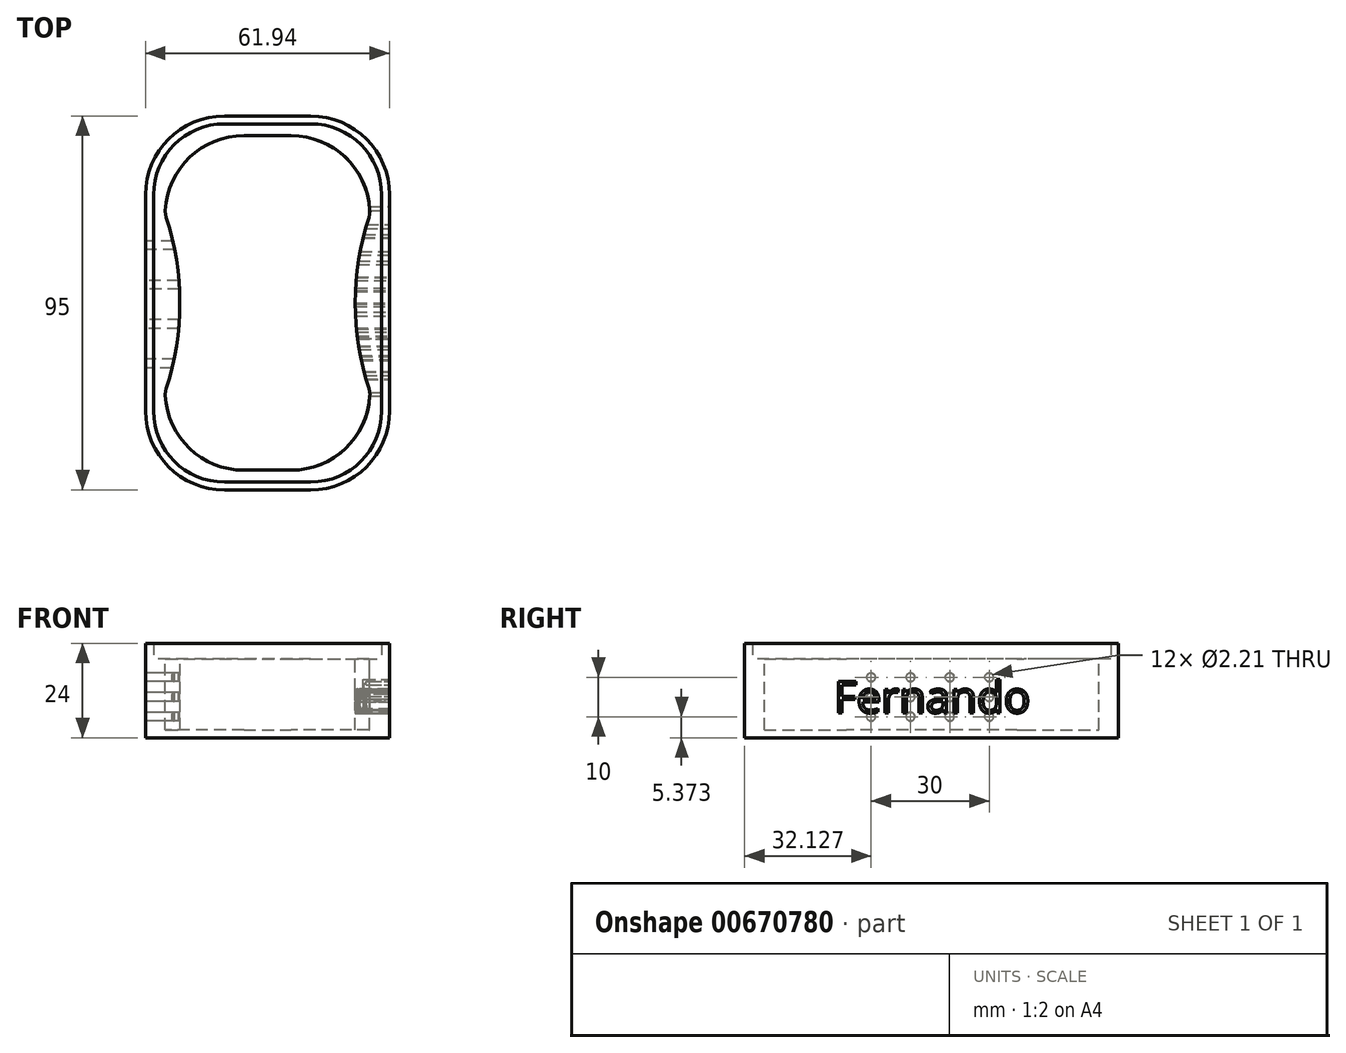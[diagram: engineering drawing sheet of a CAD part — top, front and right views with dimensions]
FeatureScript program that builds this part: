
annotation { "Feature Type Name" : "Feature", "Feature Type Description" : "" }
export const myFeature = defineFeature(function(context is Context, id is Id, definition is map)
    precondition{}
    {
        {
            var Q0;
            Q0=qCreatedBy(makeId("Top.planeOp"),FACE);
            var Q1;
            Q1 = qBodyType(qCreatedBy(id + "F1" ,EDGE), BodyType.WIRE);
            var Q2;
            Q2 = qBodyType(qCreatedBy(id + "F2" ,EDGE), BodyType.WIRE);
            cPlane(context, id + "F0", {"entities" : qUnion([Q0, Q1, Q2]), "cplaneType" : CPlaneType.OFFSET, "offset" : 20 * mm, "oppositeDirection" : true, "width" : 150 * mm, "height" : 150 * mm});
        }
        {
            var Q0;
            Q0=qCreatedBy(makeId("Top.planeOp"),FACE);
            var sketch = newSketch(context, id + "F1", { "sketchPlane" : qUnion([Q0])});
            skLineSegment(sketch, "E0", {"start": v(0, 100) * mm, "end": v(0, -100) * mm, "construction": true});
            skLineSegment(sketch, "E1", {"start": v(17.97, 4.54) * mm, "end": v(17.97, 0) * mm, "construction": true});
            skLineSegment(sketch, "E2", {"start": v(-100, 0) * mm, "end": v(100, 0) * mm, "construction": true});
            skLineSegment(sketch, "E3.bottom", {"start": v(20, 0) * mm, "end": v(32, 0) * mm});
            skLineSegment(sketch, "E3.top", {"start": v(20, 85) * mm, "end": v(32, 85) * mm});
            skPoint(sketch, "E4.visualSharp", {"position": v(0, 85) * mm});
            skArc(sketch, "E4.filletArc", {"start": v(20, 85) * mm, "mid": v(6.22, 79.5) * mm, "end": v(0.03, 66) * mm});
            skPoint(sketch, "E5.visualSharp", {"position": v(52, 85) * mm});
            skArc(sketch, "E5.filletArc", {"start": v(51.97, 66) * mm, "mid": v(45.78, 79.5) * mm, "end": v(32, 85) * mm});
            skPoint(sketch, "E6.visualSharp", {"position": v(0, 0) * mm});
            skArc(sketch, "E6.filletArc", {"start": v(0.03, 19) * mm, "mid": v(6.22, 5.5) * mm, "end": v(20, 0) * mm});
            skPoint(sketch, "E7.visualSharp", {"position": v(52, 0) * mm});
            skArc(sketch, "E7.filletArc", {"start": v(32, 0) * mm, "mid": v(45.78, 5.5) * mm, "end": v(51.97, 19) * mm});
            skArc(sketch, "E8", {"start": v(0.27, 20.8) * mm, "mid": v(3.71, 42.5) * mm, "end": v(0.27, 64.2) * mm});
            skArc(sketch, "E9", {"start": v(51.73, 64.2) * mm, "mid": v(48.29, 42.5) * mm, "end": v(51.73, 20.8) * mm});
            skPoint(sketch, "E10.visualSharp", {"position": v(0, 65) * mm});
            skArc(sketch, "E10.filletArc", {"start": v(0.03, 66) * mm, "mid": v(0.06, 65.1) * mm, "end": v(0.27, 64.2) * mm});
            skPoint(sketch, "E11.visualSharp", {"position": v(52, 65) * mm});
            skArc(sketch, "E11.filletArc", {"start": v(51.73, 64.2) * mm, "mid": v(51.94, 65.1) * mm, "end": v(51.97, 66) * mm});
            skPoint(sketch, "E12.visualSharp", {"position": v(52, 20) * mm});
            skArc(sketch, "E12.filletArc", {"start": v(51.97, 19) * mm, "mid": v(51.94, 19.9) * mm, "end": v(51.73, 20.8) * mm});
            skPoint(sketch, "E13.visualSharp", {"position": v(0, 20) * mm});
            skArc(sketch, "E13.filletArc", {"start": v(0.27, 20.8) * mm, "mid": v(0.06, 19.9) * mm, "end": v(0.03, 19) * mm});
            skSolve(sketch);
        }
        {
            var Q0;
            Q0=qCreatedBy(id+"F0.planeOp",FACE);
            var sketch = newSketch(context, id + "F2", { "sketchPlane" : qUnion([Q0])});
            skLineSegment(sketch, "E14.bottom", {"start": v(-4.97, 90) * mm, "end": v(56.97, 90) * mm});
            skLineSegment(sketch, "E14.top", {"start": v(-4.97, -5) * mm, "end": v(56.97, -5) * mm});
            skLineSegment(sketch, "E14.left", {"start": v(-4.97, 90) * mm, "end": v(-4.97, -5) * mm});
            skLineSegment(sketch, "E14.right", {"start": v(56.97, 90) * mm, "end": v(56.97, -5) * mm});
            skSolve(sketch);
        }
        {
            var Q0;
            Q0 = qSketchRegion(id + "F2", true);
            extrude(context, id + "F3", {"entities" : qUnion([Q0]), "depth" : 20 * mm, "offsetDistance" : 25 * mm});
        }
        {
            var Q0;
            Q0=makeQuery(id+"F3.opExtrude","SWEPT_EDGE",EDGE,{"disambiguationData":[OSD([sQuery(id+"F2.wireOp",EDGE,"E14.bottom"),sQuery(id+"F2.wireOp",EDGE,"E14.left")])]});
            var Q1;
            Q1=makeQuery(id+"F3.opExtrude","SWEPT_EDGE",EDGE,{"disambiguationData":[OSD([sQuery(id+"F2.wireOp",EDGE,"E14.top"),sQuery(id+"F2.wireOp",EDGE,"E14.left")])]});
            var Q2;
            Q2=makeQuery(id+"F3.opExtrude","SWEPT_EDGE",EDGE,{"disambiguationData":[OSD([sQuery(id+"F2.wireOp",EDGE,"E14.top"),sQuery(id+"F2.wireOp",EDGE,"E14.right")])]});
            var Q3;
            Q3=makeQuery(id+"F3.opExtrude","SWEPT_EDGE",EDGE,{"disambiguationData":[OSD([sQuery(id+"F2.wireOp",EDGE,"E14.bottom"),sQuery(id+"F2.wireOp",EDGE,"E14.right")])]});
            fillet(context, id + "F4", {"entities" : qUnion([Q0, Q1, Q2, Q3]), "radius" : 20 * mm, "tangentPropagation" : true, "allowEdgeOverflow" : false});
        }
        {
            var Q0;
            Q0 = qSketchRegion(id + "F1", true);
            extrude(context, id + "F5", {"entities" : qUnion([Q0]), "operationType" : NewBodyOperationType.REMOVE, "oppositeDirection" : true, "depth" : 18 * mm, "offsetDistance" : 25 * mm});
        }
        {
            var Q0;
            Q0=makeQuery(id+"F3.opExtrude","SWEPT_FACE",FACE,{"disambiguationData":[OSD([sQuery(id+"F2.wireOp",EDGE,"E14.right")])]});
            var sketch = newSketch(context, id + "F6", { "sketchPlane" : qUnion([Q0])});
            skText(sketch, "E15", { "text": "Fernando\n", "fontName": "OpenSans-Regular.ttf"});
            const initialGuessF6  = {"E15": [0.0177, -0.01364, 1, 0, 0.008]};
            skSetInitialGuess(sketch, initialGuessF6);
            skSolve(sketch);
        }
        {
            var Q0;
            Q0 = qSketchRegion(id + "F6", true);
            extrude(context, id + "F7", {"entities" : qUnion([Q0]), "operationType" : NewBodyOperationType.REMOVE, "oppositeDirection" : true, "depth" : 18 * mm, "offsetDistance" : 25 * mm});
        }
        {
            var Q0;
            Q0=makeQuery(id+"F3.opExtrude","SWEPT_FACE",FACE,{"disambiguationData":[OSD([sQuery(id+"F2.wireOp",EDGE,"E14.left")])]});
            var sketch = newSketch(context, id + "F8", { "sketchPlane" : qUnion([Q0])});
            skCircle(sketch, "E16", {"center": v(-57.13, -14.63) * mm, "radius": 1.1 * mm});
            skCircle(sketch, "E17.0.1.0", {"center": v(-57.13, -9.63) * mm, "radius": 1.1 * mm});
            skCircle(sketch, "E17.0.2.0", {"center": v(-57.13, -4.63) * mm, "radius": 1.1 * mm});
            skCircle(sketch, "E17.1.0.0", {"center": v(-47.13, -14.63) * mm, "radius": 1.1 * mm});
            skCircle(sketch, "E17.1.1.0", {"center": v(-47.13, -9.63) * mm, "radius": 1.1 * mm});
            skCircle(sketch, "E17.1.2.0", {"center": v(-47.13, -4.63) * mm, "radius": 1.1 * mm});
            skCircle(sketch, "E17.2.0.0", {"center": v(-37.13, -14.63) * mm, "radius": 1.1 * mm});
            skCircle(sketch, "E17.2.1.0", {"center": v(-37.13, -9.63) * mm, "radius": 1.1 * mm});
            skCircle(sketch, "E17.2.2.0", {"center": v(-37.13, -4.63) * mm, "radius": 1.1 * mm});
            skCircle(sketch, "E17.3.0.0", {"center": v(-27.13, -14.63) * mm, "radius": 1.1 * mm});
            skCircle(sketch, "E17.3.1.0", {"center": v(-27.13, -9.63) * mm, "radius": 1.1 * mm});
            skCircle(sketch, "E17.3.2.0", {"center": v(-27.13, -4.63) * mm, "radius": 1.1 * mm});
            skLineSegment(sketch, "E17.direction1", {"start": v(-57.13, -14.63) * mm, "end": v(-47.13, -14.63) * mm, "construction": true});
            skLineSegment(sketch, "E17.direction2", {"start": v(-57.13, -14.63) * mm, "end": v(-57.13, -9.63) * mm, "construction": true});
            skSolve(sketch);
        }
        {
            var Q0;
            Q0 = qSketchRegion(id + "F8", true);
            extrude(context, id + "F9", {"entities" : qUnion([Q0]), "operationType" : NewBodyOperationType.REMOVE, "endBound" : BoundingType.UP_TO_NEXT, "oppositeDirection" : true, "depth" : 5 * mm, "offsetDistance" : 25 * mm});
        }
        {
            var Q0;
            Q0=makeQuery(id+"F3.opExtrude","CAP_FACE",FACE,{"disambiguationData":[OSD([sQuery(id+"F2.wireOp",EDGE,"E14.bottom"),sQuery(id+"F2.wireOp",EDGE,"E14.top"),sQuery(id+"F2.wireOp",EDGE,"E14.left"),sQuery(id+"F2.wireOp",EDGE,"E14.right")])],"isStart":false});
            var sketch = newSketch(context, id + "F10", { "sketchPlane" : qUnion([Q0])});
            skArc(sketch, "E18.0", {"start": v(15.03, 88) * mm, "mid": v(2.3, 82.73) * mm, "end": v(-2.97, 70) * mm});
            skLineSegment(sketch, "E18.1", {"start": v(36.97, 88) * mm, "end": v(15.03, 88) * mm});
            skLineSegment(sketch, "E18.2", {"start": v(-2.97, 70) * mm, "end": v(-2.97, 15) * mm});
            skArc(sketch, "E18.3", {"start": v(54.97, 70) * mm, "mid": v(49.7, 82.73) * mm, "end": v(36.97, 88) * mm});
            skArc(sketch, "E18.4", {"start": v(-2.97, 15) * mm, "mid": v(2.3, 2.27) * mm, "end": v(15.03, -3) * mm});
            skLineSegment(sketch, "E18.5", {"start": v(15.03, -3) * mm, "end": v(36.97, -3) * mm});
            skArc(sketch, "E18.6", {"start": v(36.97, -3) * mm, "mid": v(49.7, 2.27) * mm, "end": v(54.97, 15) * mm});
            skLineSegment(sketch, "E18.7", {"start": v(54.97, 15) * mm, "end": v(54.97, 70) * mm});
            skSolve(sketch);
        }
        {
            var Q0;
            Q0=makeQuery(id+"F10.imprint","IMPRINT",FACE,{"disambiguationData":[TD([[makeQuery(id+"F10.imprint","IMPRINT",EDGE,{"derivedFrom":sQuery(id+"F10.wireOp",EDGE,"E18.0")}),-1.0]])]});
            extrude(context, id + "F11", {"entities" : qUnion([Q0]), "operationType" : NewBodyOperationType.ADD, "depth" : 4 * mm, "offsetDistance" : 25 * mm});
        }
    });
